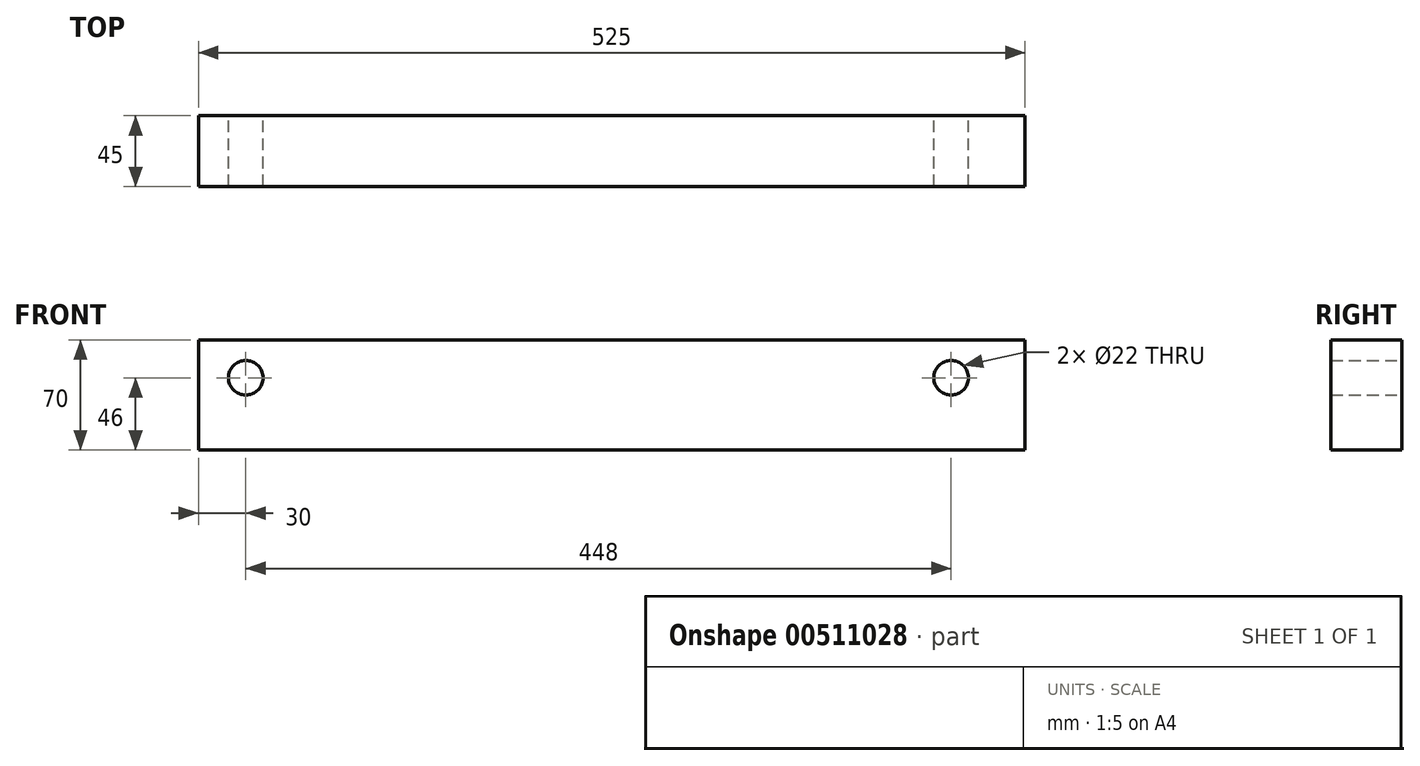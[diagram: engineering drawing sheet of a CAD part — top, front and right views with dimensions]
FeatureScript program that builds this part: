
annotation { "Feature Type Name" : "Feature", "Feature Type Description" : "" }
export const myFeature = defineFeature(function(context is Context, id is Id, definition is map)
    precondition{}
    {
        {
            var Q0;
            Q0=qCreatedBy(makeId("Front.planeOp"),FACE);
            var sketch = newSketch(context, id + "F0", { "sketchPlane" : qUnion([Q0])});
            skLineSegment(sketch, "E0.bottom", {"start": v(0, 0) * mm, "end": v(-525, 0) * mm});
            skLineSegment(sketch, "E0.top", {"start": v(0, -70) * mm, "end": v(-525, -70) * mm});
            skLineSegment(sketch, "E0.left", {"start": v(0, 0) * mm, "end": v(0, -70) * mm});
            skLineSegment(sketch, "E0.right", {"start": v(-525, 0) * mm, "end": v(-525, -70) * mm});
            skSolve(sketch);
        }
        {
            var Q0;
            Q0=qSketchRegion(id+"F0",true);
            extrude(context, id + "F1", {"entities" : qUnion([Q0]), "depth" : 45 * mm});
        }
        {
            var Q0;
            Q0=makeQuery(id+"F1.opExtrude","CAP_FACE",FACE,{"disambiguationData":[OSD([sQuery(id+"F0.wireOp",EDGE,"E0.bottom"),sQuery(id+"F0.wireOp",EDGE,"E0.top"),sQuery(id+"F0.wireOp",EDGE,"E0.left"),sQuery(id+"F0.wireOp",EDGE,"E0.right")])],"isStart":true});
            var sketch = newSketch(context, id + "F2", { "sketchPlane" : qUnion([Q0])});
            skCircle(sketch, "E1", {"center": v(495, -24) * mm, "radius": 11 * mm});
            skSolve(sketch);
        }
        {
            var Q0;
            Q0=qSketchRegion(id+"F2",true);
            extrude(context, id + "F3", {"entities" : qUnion([Q0]), "operationType" : NewBodyOperationType.REMOVE, "endBound" : BoundingType.THROUGH_ALL, "oppositeDirection" : true, "depth" : 25 * mm});
        }
        {
            var Q0;
            Q0=makeQuery(id+"F1.opExtrude","CAP_FACE",FACE,{"disambiguationData":[OSD([sQuery(id+"F0.wireOp",EDGE,"E0.bottom"),sQuery(id+"F0.wireOp",EDGE,"E0.top"),sQuery(id+"F0.wireOp",EDGE,"E0.left"),sQuery(id+"F0.wireOp",EDGE,"E0.right")])],"isStart":true});
            var sketch = newSketch(context, id + "F4", { "sketchPlane" : qUnion([Q0])});
            skCircle(sketch, "E2", {"center": v(47, -24) * mm, "radius": 11 * mm});
            skSolve(sketch);
        }
        {
            var Q0;
            Q0=qSketchRegion(id+"F4",true);
            extrude(context, id + "F5", {"entities" : qUnion([Q0]), "operationType" : NewBodyOperationType.REMOVE, "endBound" : BoundingType.THROUGH_ALL, "oppositeDirection" : true, "depth" : 25 * mm});
        }
    });
